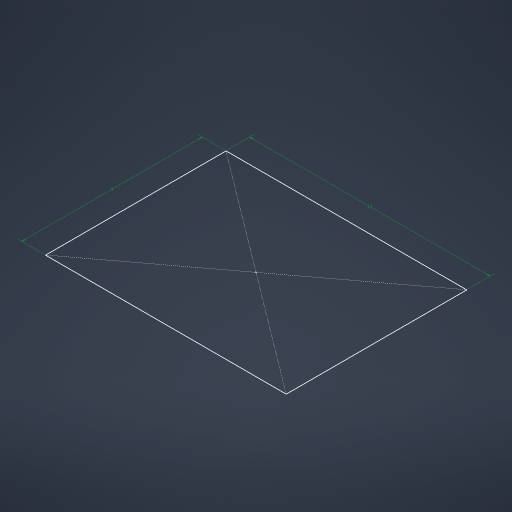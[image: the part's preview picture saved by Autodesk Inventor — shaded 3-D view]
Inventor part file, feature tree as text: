
AUTODESK INVENTOR PART (.ipt)
format: ipt  version: 2024.3 (Build 283343000, 343)  size: 165,376 bytes
history: native  units: in
note: dims shown in document units (in); Inventor stores cm internally (conversion verified against a paired STEP export)
features: sketch x1
ambient origin geometry x8: Origin, YZ Plane, XZ Plane, XY Plane, X Axis, Y Axis, Z Axis, Center Point
feature tree (1):
  sketch  "Sketch11"  dims[d42=472.4409in d43=354.3307in]
